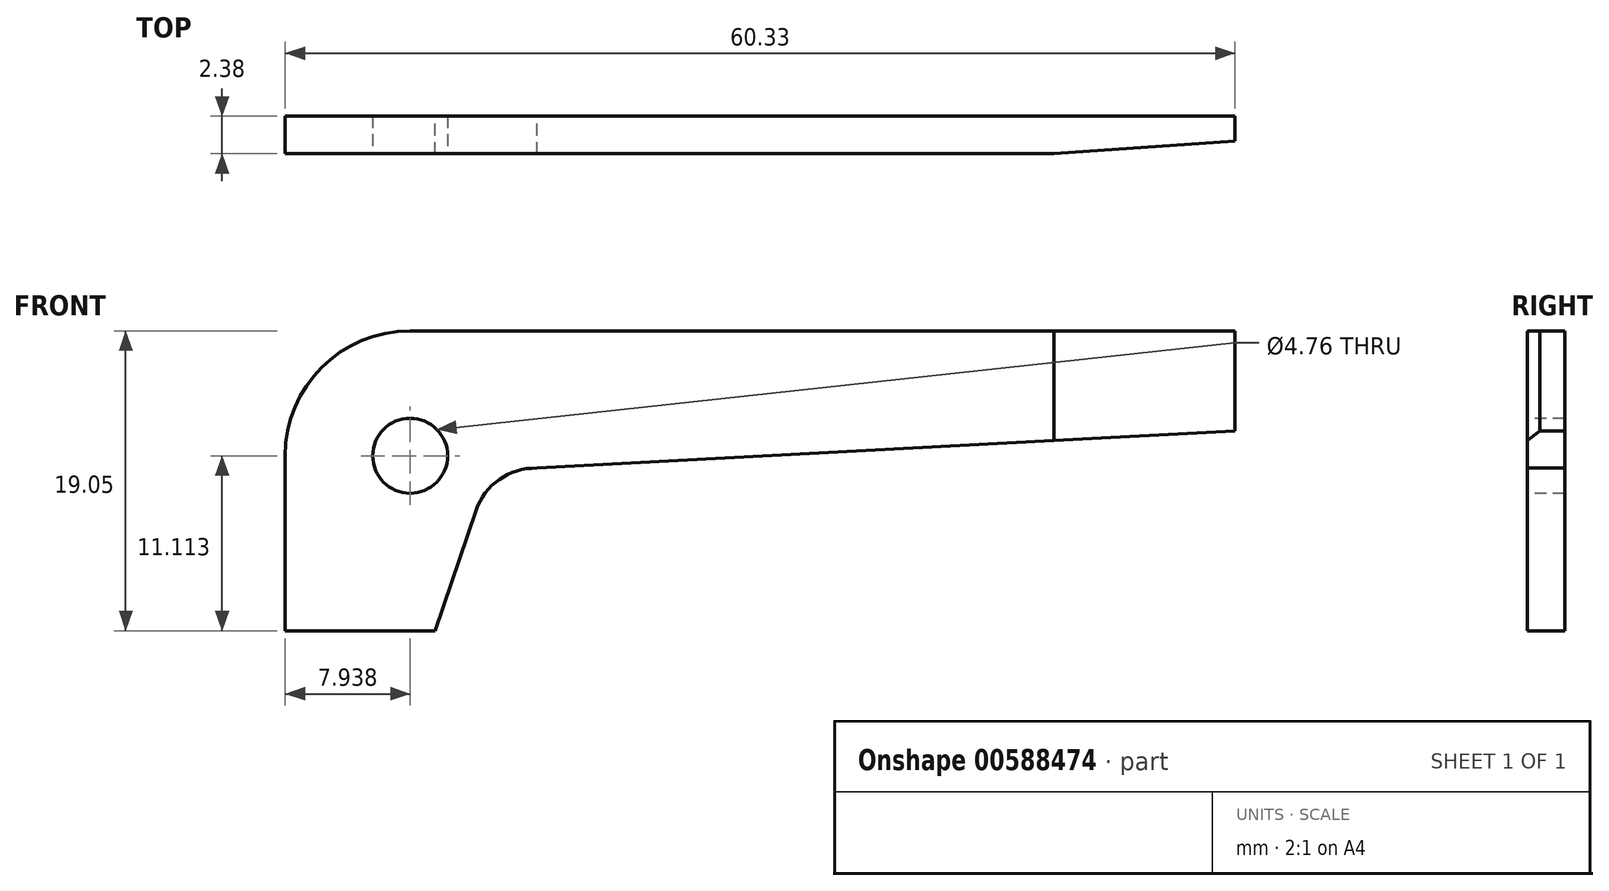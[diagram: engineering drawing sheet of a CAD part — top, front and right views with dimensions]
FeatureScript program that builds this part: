
annotation { "Feature Type Name" : "Feature", "Feature Type Description" : "" }
export const myFeature = defineFeature(function(context is Context, id is Id, definition is map)
    precondition{}
    {
        {
            var Q0;
            Q0=qCreatedBy(makeId("Front.planeOp"),FACE);
            var sketch = newSketch(context, id + "F0", { "sketchPlane" : qUnion([Q0])});
            skLineSegment(sketch, "E0.top", {"start": v(7.94, 19.05) * mm, "end": v(60.33, 19.05) * mm});
            skLineSegment(sketch, "E1", {"start": v(9.52, 0) * mm, "end": v(12.11, 7.63) * mm});
            skLineSegment(sketch, "E2", {"start": v(15.98, 10.32) * mm, "end": v(60.33, 12.7) * mm});
            skLineSegment(sketch, "E3", {"start": v(9.52, 0) * mm, "end": v(0, 0) * mm});
            skLineSegment(sketch, "E4", {"start": v(0, 0) * mm, "end": v(0, 11.11) * mm});
            skLineSegment(sketch, "E5", {"start": v(60.33, 12.7) * mm, "end": v(60.33, 19.05) * mm});
            skArc(sketch, "E6", {"start": v(15.98, 10.32) * mm, "mid": v(13.6, 9.61) * mm, "end": v(12.11, 7.63) * mm});
            skPoint(sketch, "E7.visualSharp", {"position": v(0, 19.05) * mm});
            skArc(sketch, "E7.filletArc", {"start": v(7.94, 19.05) * mm, "mid": v(2.32, 16.73) * mm, "end": v(0, 11.11) * mm});
            skSolve(sketch);
        }
        {
            var Q0;
            Q0 = qSketchRegion(id + "F0", true);
            extrude(context, id + "F1", {"entities" : qUnion([Q0]), "depth" : 2.38 * mm, "offsetDistance" : 25.4 * mm});
        }
        {
            var Q0;
            Q0=makeQuery(id+"F1.opExtrude","CAP_FACE",FACE,{"disambiguationData":[OSD([sQuery(id+"F0.wireOp",EDGE,"E0.top"),sQuery(id+"F0.wireOp",EDGE,"E1"),sQuery(id+"F0.wireOp",EDGE,"E2"),sQuery(id+"F0.wireOp",EDGE,"E3"),sQuery(id+"F0.wireOp",EDGE,"E4"),sQuery(id+"F0.wireOp",EDGE,"E5"),sQuery(id+"F0.wireOp",EDGE,"E6"),sQuery(id+"F0.wireOp",EDGE,"E7.filletArc")])],"isStart":false});
            var sketch = newSketch(context, id + "F2", { "sketchPlane" : qUnion([Q0])});
            skCircle(sketch, "E8", {"center": v(7.94, 11.11) * mm, "radius": 2.38 * mm});
            skSolve(sketch);
        }
        {
            var Q0;
            Q0=makeQuery(id+"F2.imprint","IMPRINT",FACE,{"disambiguationData":[TD([[makeQuery(id+"F2.imprint","IMPRINT",EDGE,{"derivedFrom":sQuery(id+"F2.wireOp",EDGE,"E8")}),1.0]])]});
            extrude(context, id + "F3", {"entities" : qUnion([Q0]), "operationType" : NewBodyOperationType.REMOVE, "oppositeDirection" : true, "depth" : 25.4 * mm, "offsetDistance" : 25.4 * mm});
        }
        {
            var Q0;
            Q0=makeQuery(id+"F1.opExtrude","SWEPT_FACE",FACE,{"disambiguationData":[OSD([sQuery(id+"F0.wireOp",EDGE,"E0.top")])]});
            var sketch = newSketch(context, id + "F4", { "sketchPlane" : qUnion([Q0])});
            skLineSegment(sketch, "E9", {"start": v(48.83, 0) * mm, "end": v(60.33, -0.8) * mm});
            skLineSegment(sketch, "E10", {"start": v(60.33, -0.8) * mm, "end": v(48.83, 0) * mm});
            skLineSegment(sketch, "E11.MirrorCS", {"start": v(60.33, -1.59) * mm, "end": v(48.83, -2.38) * mm});
            skSolve(sketch);
        }
        {
            var Q0;
            Q0 = qSketchRegion(id + "F4", true);
            var Q1;
            {var subQ0=sQuery(id+"F4.wireOp",EDGE,"E10");Q1=makeQuery(id+"F4.imprint","IMPRINT",FACE,{"disambiguationData":[TD([[makeQuery(id+"F4.imprint","IMPRINT",EDGE,{"derivedFrom":subQ0}),-1.0]])]});}
            var Q2;
            {var subQ0=sQuery(id+"F4.wireOp",EDGE,"E11.MirrorCS");Q2=makeQuery(id+"F4.imprint","IMPRINT",FACE,{"disambiguationData":[TD([[makeQuery(id+"F4.imprint","IMPRINT",EDGE,{"derivedFrom":subQ0}),1.0]])]});}
            extrude(context, id + "F5", {"entities" : qUnion([Q0, Q1, Q2]), "operationType" : NewBodyOperationType.REMOVE, "oppositeDirection" : true, "depth" : 25.4 * mm, "offsetDistance" : 25.4 * mm});
        }
    });
